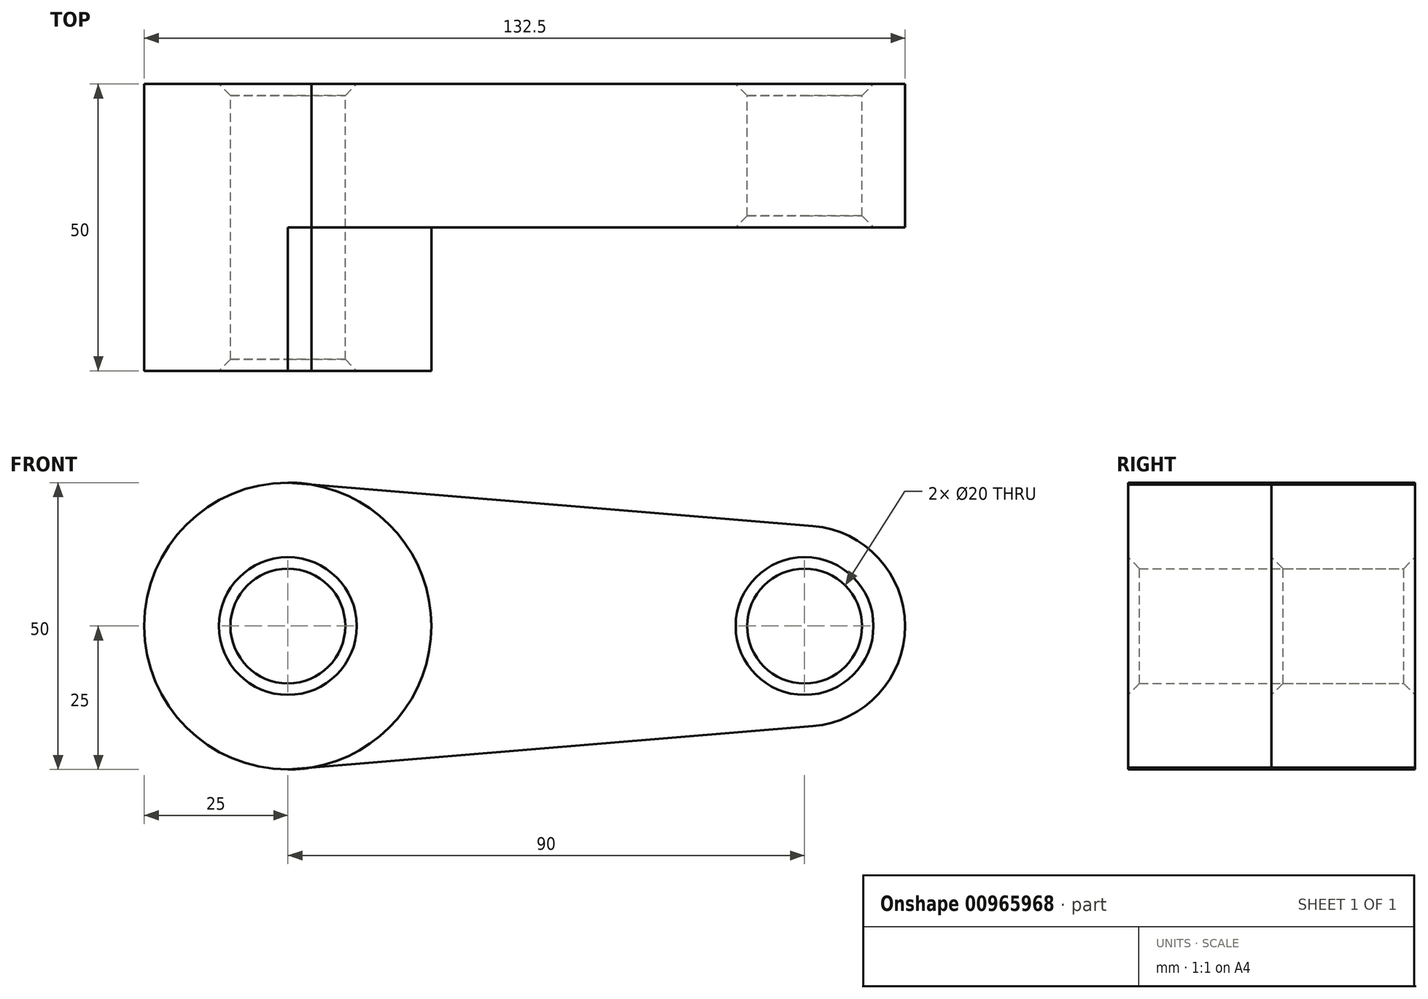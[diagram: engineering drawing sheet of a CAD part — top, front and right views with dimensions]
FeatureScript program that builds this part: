
annotation { "Feature Type Name" : "Feature", "Feature Type Description" : "" }
export const myFeature = defineFeature(function(context is Context, id is Id, definition is map)
    precondition{}
    {
        {
            var Q0;
            Q0=qCreatedBy(makeId("Front.planeOp"),FACE);
            var sketch = newSketch(context, id + "F0", { "sketchPlane" : qUnion([Q0])});
            skCircle(sketch, "E0", {"center": v(0, 0) * mm, "radius": 25 * mm});
            skCircle(sketch, "E1", {"center": v(90, 0) * mm, "radius": 17.5 * mm});
            skLineSegment(sketch, "E2", {"start": v(0, 25) * mm, "end": v(91.44, 17.44) * mm});
            skLineSegment(sketch, "E3", {"start": v(0, -25) * mm, "end": v(91.44, -17.44) * mm});
            skCircle(sketch, "E4", {"center": v(0, 0) * mm, "radius": 10 * mm});
            skCircle(sketch, "E5", {"center": v(90, 0) * mm, "radius": 10 * mm});
            skSolve(sketch);
        }
        {
            var Q0;
            Q0=qSketchRegion(id+"F0",true);
            extrude(context, id + "F1", {"entities" : qUnion([Q0]), "depth" : 25 * mm, "offsetDistance" : 25 * mm});
        }
        {
            var Q0;
            Q0=makeQuery(id+"F0.imprint","IMPRINT",FACE,{"disambiguationData":[TD([[makeQuery(id+"F0.imprint","IMPRINT",EDGE,{"derivedFrom":sQuery(id+"F0.wireOp",EDGE,"E4")}),-1.0]])]});
            extrude(context, id + "F2", {"entities" : qUnion([Q0]), "operationType" : NewBodyOperationType.ADD, "depth" : 50 * mm, "offsetDistance" : 25 * mm});
        }
        {
            var Q0;
            {var subQ0=sQuery(id+"F0.wireOp",EDGE,"E4");Q0=makeQuery(id+"F2.boolean.opBoolean","MERGE",FACE,{"derivedFrom":[makeQuery(id+"F1.opExtrude","SWEPT_FACE",FACE,{"disambiguationData":[OSD([subQ0])]}),makeQuery(id+"F2.opExtrude","SWEPT_FACE",FACE,{"disambiguationData":[OSD([subQ0])]})]});}
            var Q1;
            {var subQ0=sQuery(id+"F0.wireOp",EDGE,"E0");Q1=makeQuery(id+"F2.opExtrude","CAP_EDGE",EDGE,{"disambiguationData":[OSD([subQ0]),TDD([makeQuery(id+"F0.imprint","IMPRINT",EDGE,{"disambiguationData":[TD([[makeQuery(id+"F0.imprint","INTERSECT",VERTEX,{"disambiguationData":[OD(0.0)],"derivedFrom":[subQ0,sQuery(id+"F0.wireOp",EDGE,"E2")]}),-1.0]])],"derivedFrom":subQ0})])],"isStart":false});}
            var Q2;
            Q2=makeQuery(id+"F1.opExtrude","SWEPT_FACE",FACE,{"disambiguationData":[OSD([sQuery(id+"F0.wireOp",EDGE,"E5")])]});
            chamfer(context, id + "F3", {"entities" : qUnion([Q0, Q1, Q2]), "width" : 2 * mm, "tangentPropagation" : true});
        }
    });
